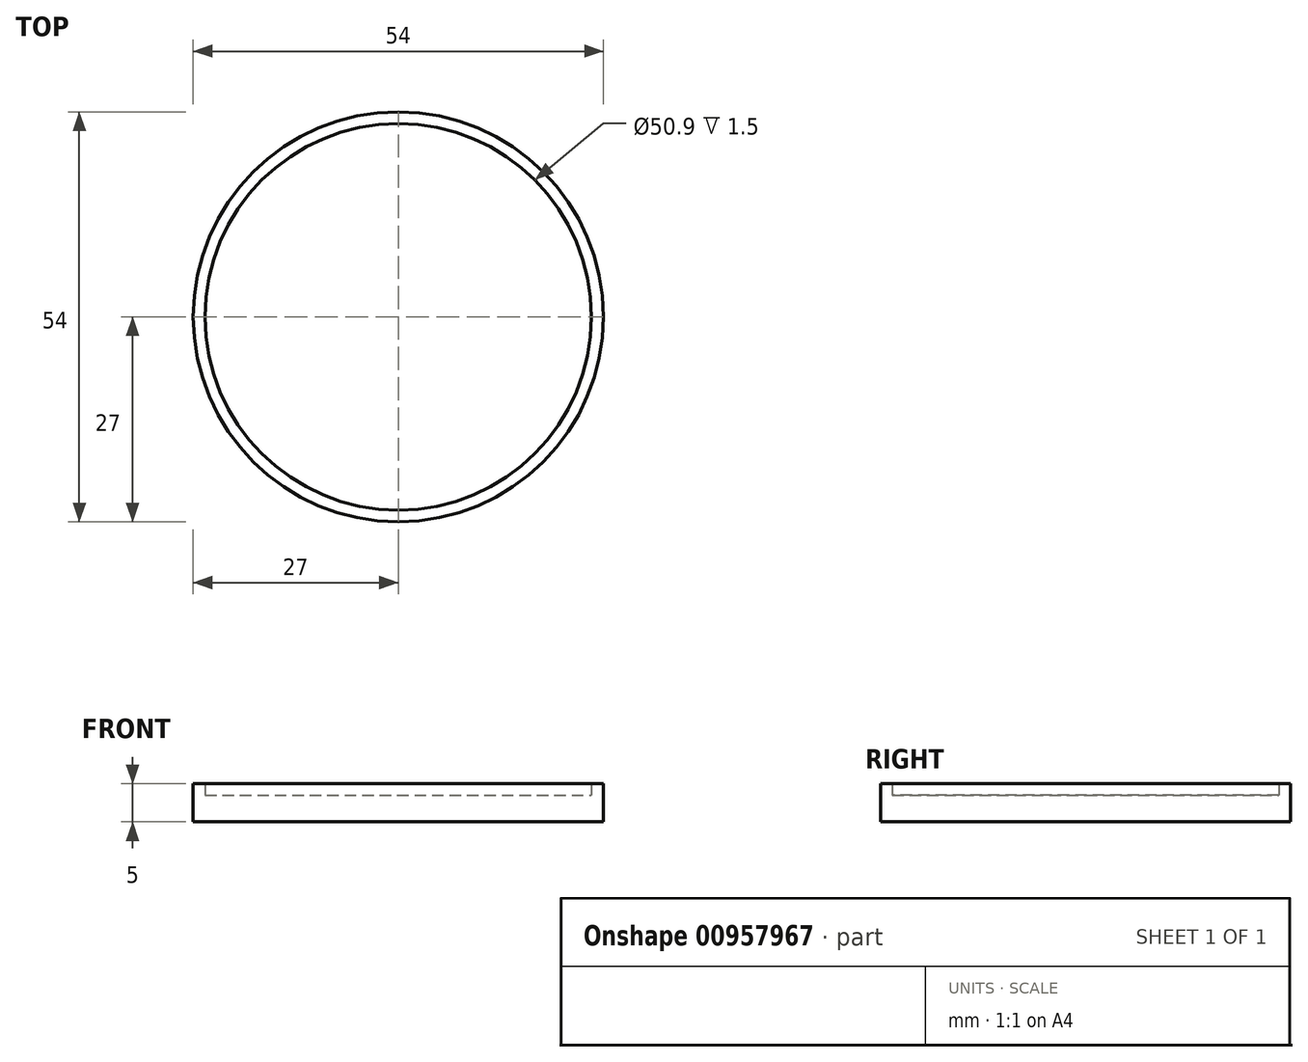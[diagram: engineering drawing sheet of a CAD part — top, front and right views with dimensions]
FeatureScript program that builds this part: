
annotation { "Feature Type Name" : "Feature", "Feature Type Description" : "" }
export const myFeature = defineFeature(function(context is Context, id is Id, definition is map)
    precondition{}
    {
        {
            var Q0;
            Q0=qCreatedBy(makeId("Front.planeOp"),FACE);
            var sketch = newSketch(context, id + "F0", { "sketchPlane" : qUnion([Q0])});
            skLineSegment(sketch, "E0.bottom", {"start": v(-27, 5) * mm, "end": v(27, 5) * mm});
            skLineSegment(sketch, "E0.top", {"start": v(-27, 0) * mm, "end": v(27, 0) * mm});
            skLineSegment(sketch, "E0.left", {"start": v(-27, 5) * mm, "end": v(-27, 0) * mm});
            skLineSegment(sketch, "E0.right", {"start": v(27, 5) * mm, "end": v(27, 0) * mm});
            skLineSegment(sketch, "E1.bottom", {"start": v(-25.45, 5) * mm, "end": v(25.45, 5) * mm});
            skLineSegment(sketch, "E1.top", {"start": v(-25.45, 3.5) * mm, "end": v(25.45, 3.5) * mm});
            skLineSegment(sketch, "E1.left", {"start": v(-25.45, 5) * mm, "end": v(-25.45, 3.5) * mm});
            skLineSegment(sketch, "E1.right", {"start": v(25.45, 5) * mm, "end": v(25.45, 3.5) * mm});
            skLineSegment(sketch, "E2", {"start": v(0, 0) * mm, "end": v(0, 3.5) * mm});
            skSolve(sketch);
        }
        {
            var Q0;
            {var subQ0=sQuery(id+"F0.wireOp",EDGE,"E0.left");Q0=makeQuery(id+"F0.imprint","IMPRINT",FACE,{"disambiguationData":[TD([[makeQuery(id+"F0.imprint","IMPRINT",EDGE,{"derivedFrom":subQ0}),1.0]])]});}
            var Q1;
            Q1=sQuery(id+"F0.wireOp",EDGE,"E2");
            revolve(context, id + "F1", {"surfaceOperationType" : NewSurfaceOperationType.NEW, "entities" : qUnion([Q0]), "axis" : qUnion([Q1]), "revolveType" : RevolveType.FULL});
        }
    });
